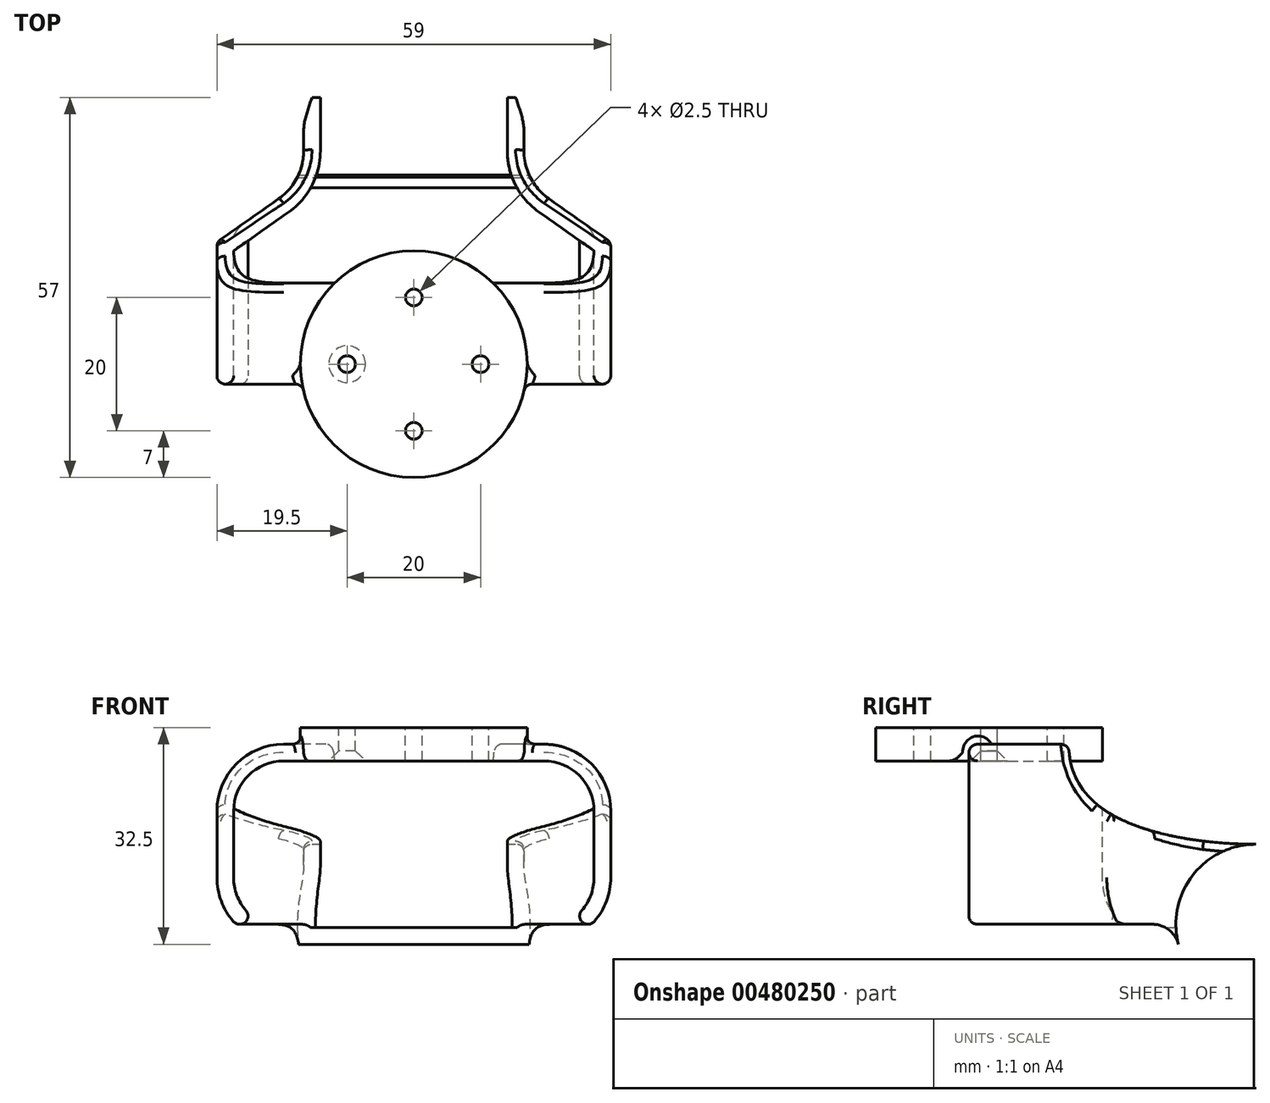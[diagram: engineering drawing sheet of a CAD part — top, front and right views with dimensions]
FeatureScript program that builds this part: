
annotation { "Feature Type Name" : "Feature", "Feature Type Description" : "" }
export const myFeature = defineFeature(function(context is Context, id is Id, definition is map)
    precondition{}
    {
        {
            var Q0;
            Q0=qCreatedBy(makeId("Right.planeOp"),FACE);
            var sketch = newSketch(context, id + "F0", { "sketchPlane" : qUnion([Q0])});
            skCircle(sketch, "E0", {"center": v(8, -12) * mm, "radius": 12 * mm});
            skCircle(sketch, "E1", {"center": v(8, -12) * mm, "radius": 9.5 * mm});
            skSolve(sketch);
        }
        {
            var Q0;
            Q0 = qSketchRegion(id + "F0", true);
            extrude(context, id + "F1", {"entities" : qUnion([Q0]), "endBound" : BoundingType.SYMMETRIC, "depth" : 50 * mm});
        }
        {
            var Q0;
            Q0=qCreatedBy(makeId("Top.planeOp"),FACE);
            var sketch = newSketch(context, id + "F2", { "sketchPlane" : qUnion([Q0])});
            skLineSegment(sketch, "E2", {"start": v(27, -15) * mm, "end": v(27, -35) * mm});
            skArc(sketch, "E3", {"start": v(14, 0) * mm, "mid": v(15.28, -5.22) * mm, "end": v(18.81, -9.26) * mm});
            skLineSegment(sketch, "E4", {"start": v(18.81, -9.26) * mm, "end": v(27, -15) * mm});
            skLineSegment(sketch, "E5", {"start": v(14, 0) * mm, "end": v(14, 20) * mm});
            skLineSegment(sketch, "E6", {"start": v(14, 20) * mm, "end": v(0, 20) * mm});
            skLineSegment(sketch, "E7.0", {"start": v(29.5, 22.5) * mm, "end": v(0, 22.5) * mm});
            skLineSegment(sketch, "E7.1", {"start": v(29.5, 22.5) * mm, "end": v(29.5, -35) * mm});
            skLineSegment(sketch, "E8", {"start": v(0, 22.5) * mm, "end": v(0, -35) * mm});
            skLineSegment(sketch, "E9", {"start": v(0, -35) * mm, "end": v(29.5, -35) * mm});
            skLineSegment(sketch, "E10.MirrorCS", {"start": v(-29.5, 22.5) * mm, "end": v(0, 22.5) * mm});
            skLineSegment(sketch, "E11.MirrorCS", {"start": v(-29.5, 22.5) * mm, "end": v(-29.5, -35) * mm});
            skLineSegment(sketch, "E12.MirrorCS", {"start": v(0, -35) * mm, "end": v(-29.5, -35) * mm});
            skSolve(sketch);
        }
        {
            var Q0;
            Q0 = qSketchRegion(id + "F2", true);
            extrude(context, id + "F3", {"entities" : qUnion([Q0]), "endBound" : BoundingType.SYMMETRIC, "depth" : 30 * mm});
        }
        {
            var Q0;
            Q0=makeQuery(id+"F3.opExtrude","CAP_EDGE",EDGE,{"disambiguationData":[OSD([sQuery(id+"F2.wireOp",EDGE,"E7.1")])],"isStart":false});
            var Q1;
            Q1=makeQuery(id+"F3.opExtrude","CAP_EDGE",EDGE,{"disambiguationData":[OSD([sQuery(id+"F2.wireOp",EDGE,"E7.1")])],"isStart":true});
            var Q2;
            Q2=makeQuery(id+"F3.opExtrude","CAP_EDGE",EDGE,{"disambiguationData":[OSD([sQuery(id+"F2.wireOp",EDGE,"E11.MirrorCS")])],"isStart":false});
            var Q3;
            Q3=makeQuery(id+"F3.opExtrude","CAP_EDGE",EDGE,{"disambiguationData":[OSD([sQuery(id+"F2.wireOp",EDGE,"E11.MirrorCS")])],"isStart":true});
            fillet(context, id + "F4", {"entities" : qUnion([Q0, Q1, Q2, Q3]), "radius" : 10 * mm, "tangentPropagation" : true, "allowEdgeOverflow" : false});
        }
        {
            var Q0;
            Q0=qCreatedBy(makeId("Top.planeOp"),FACE);
            var sketch = newSketch(context, id + "F5", { "sketchPlane" : qUnion([Q0])});
            skLineSegment(sketch, "E13", {"start": v(27, -15) * mm, "end": v(27, -35) * mm});
            skArc(sketch, "E14", {"start": v(14, 0) * mm, "mid": v(15.28, -5.22) * mm, "end": v(18.81, -9.26) * mm});
            skLineSegment(sketch, "E15", {"start": v(18.81, -9.26) * mm, "end": v(27, -15) * mm});
            skLineSegment(sketch, "E16", {"start": v(14, 0) * mm, "end": v(14, 22.5) * mm});
            skLineSegment(sketch, "E17.0", {"start": v(16.5, 0) * mm, "end": v(16.5, 22.5) * mm});
            skArc(sketch, "E17.1", {"start": v(16.5, 0) * mm, "mid": v(17.5, -4.06) * mm, "end": v(20.25, -7.21) * mm});
            skLineSegment(sketch, "E17.2", {"start": v(20.25, -7.21) * mm, "end": v(29.5, -13.7) * mm});
            skLineSegment(sketch, "E18", {"start": v(16.5, 22.5) * mm, "end": v(29.5, 22.5) * mm});
            skLineSegment(sketch, "E19", {"start": v(29.5, 22.5) * mm, "end": v(29.5, -13.7) * mm});
            skLineSegment(sketch, "E20.MirrorCS", {"start": v(-16.5, 0) * mm, "end": v(-16.5, 22.5) * mm});
            skLineSegment(sketch, "E21.MirrorCS", {"start": v(-16.5, 22.5) * mm, "end": v(-29.5, 22.5) * mm});
            skLineSegment(sketch, "E22.MirrorCS", {"start": v(-29.5, 22.5) * mm, "end": v(-29.5, -13.7) * mm});
            skArc(sketch, "E23.MirrorCS", {"start": v(-16.5, 0) * mm, "mid": v(-17.5, -4.06) * mm, "end": v(-20.25, -7.21) * mm});
            skLineSegment(sketch, "E24.MirrorCS", {"start": v(-20.25, -7.21) * mm, "end": v(-29.5, -13.7) * mm});
            skSolve(sketch);
        }
        {
            var Q0;
            Q0 = qSketchRegion(id + "F5", true);
            extrude(context, id + "F6", {"entities" : qUnion([Q0]), "operationType" : NewBodyOperationType.REMOVE, "endBound" : BoundingType.SYMMETRIC, "oppositeDirection" : true, "depth" : 50 * mm});
        }
        {
            var Q0;
            {var subQ0=makeQuery(id+"F3.opExtrude","SWEPT_FACE",FACE,{"disambiguationData":[OSD([sQuery(id+"F2.wireOp",EDGE,"E9")])]});Q0=makeQuery(id+"F3nsgiuGHSw1DEI_1.boolean.opBoolean","MERGE",FACE,{"derivedFrom":[subQ0,makeQuery(id+"F3nsgiuGHSw1DEI_1.opPattern","COPY",FACE,{"derivedFrom":subQ0,"instanceName":"1"})]});}
            shell(context, id + "F7", {"entities" : qUnion([Q0]), "thickness" : 2.5 * mm});
        }
        {
            var Q0;
            Q0=qCreatedBy(makeId("Right.planeOp"),FACE);
            var sketch = newSketch(context, id + "F8", { "sketchPlane" : qUnion([Q0])});
            skFitSpline(sketch, "E25", {"points": [v(-20, 15) * mm, v(-14.5, 5) * mm, v(8, 0) * mm], "startDerivative": vector(-1.27, -29.05) * mm, "endDerivative": vector(40.9, 0) * mm});
            skLineSegment(sketch, "E26", {"start": v(-20, 15) * mm, "end": v(-20, 23.6) * mm});
            skLineSegment(sketch, "E27", {"start": v(-20.04, 21.23) * mm, "end": v(28.46, 21.23) * mm});
            skLineSegment(sketch, "E28", {"start": v(28.46, 21.23) * mm, "end": v(28.46, -29.42) * mm});
            skLineSegment(sketch, "E29", {"start": v(28.46, -29.42) * mm, "end": v(-37.88, -29.42) * mm});
            skLineSegment(sketch, "E30", {"start": v(-37.88, -12) * mm, "end": v(-7.5, -12) * mm});
            skArc(sketch, "E31", {"start": v(-3.62, -15) * mm, "mid": v(-5.04, -12.84) * mm, "end": v(-7.5, -12) * mm});
            skLineSegment(sketch, "E32", {"start": v(-37.88, -12) * mm, "end": v(-37.88, -29.42) * mm});
            skLineSegment(sketch, "E33", {"start": v(8, 0) * mm, "end": v(8, -12) * mm});
            skCircle(sketch, "E34", {"center": v(8, -12) * mm, "radius": 12 * mm});
            skSolve(sketch);
        }
        {
            var Q0;
            Q0 = qSketchRegion(id + "F8", true);
            extrude(context, id + "F9", {"entities" : qUnion([Q0]), "operationType" : NewBodyOperationType.REMOVE, "endBound" : BoundingType.SYMMETRIC, "oppositeDirection" : true, "depth" : 60 * mm});
        }
        {
            var Q0;
            {var subQ0=sQuery(id+"F2.wireOp",EDGE,"E12.MirrorCS");var subQ1=sQuery(id+"F2.wireOp",EDGE,"E11.MirrorCS");var subQ2=sQuery(id+"F2.wireOp",EDGE,"E10.MirrorCS");var subQ3=sQuery(id+"F2.wireOp",EDGE,"E9");var subQ4=sQuery(id+"F2.wireOp",EDGE,"E7.1");var subQ5=sQuery(id+"F2.wireOp",EDGE,"E7.0");Q0=makeQuery(id+"F7.opShell","OFFSET_FACE",FACE,{"disambiguationData":[OSD([subQ5,subQ4,subQ3,subQ2,subQ1,subQ0]),TDD([makeQuery(id+"F3.opExtrude","CAP_FACE",FACE,{"disambiguationData":[OSD([subQ5,subQ4,subQ3,subQ2,subQ1,subQ0])],"isStart":false})])]});}
            var sketch = newSketch(context, id + "F10", { "sketchPlane" : qUnion([Q0])});
            skCircle(sketch, "E35", {"center": v(0, 32) * mm, "radius": 17 * mm});
            skPoint(sketch, "E35.centerSnap0", {"position": v(0, 20) * mm});
            skCircle(sketch, "E36", {"center": v(0, 32) * mm, "radius": 15 * mm, "construction": true});
            skSolve(sketch);
        }
        {
            var Q0;
            Q0 = qSketchRegion(id + "F10", true);
            extrude(context, id + "F11", {"entities" : qUnion([Q0]), "operationType" : NewBodyOperationType.ADD, "oppositeDirection" : true, "depth" : 5 * mm});
        }
        {
            var Q0;
            Q0=makeQuery(id+"F11.opExtrude","CAP_FACE",FACE,{"disambiguationData":[OSD([sQuery(id+"F10.wireOp",EDGE,"E35")])],"isStart":false});
            var sketch = newSketch(context, id + "F12", { "sketchPlane" : qUnion([Q0])});
            skCircle(sketch, "E37", {"center": v(-10, -32) * mm, "radius": 1.25 * mm});
            skLineSegment(sketch, "E38", {"start": v(-17, -32) * mm, "end": v(0, -32) * mm, "construction": true});
            skCircle(sketch, "E39.1.0", {"center": v(0, -42) * mm, "radius": 1.25 * mm});
            skCircle(sketch, "E39.2.0", {"center": v(10, -32) * mm, "radius": 1.25 * mm});
            skCircle(sketch, "E39.3.0", {"center": v(0, -22) * mm, "radius": 1.25 * mm});
            skPoint(sketch, "E39.center", {"position": v(0, -32) * mm});
            skSolve(sketch);
        }
        {
            var Q0;
            Q0 = qSketchRegion(id + "F12", true);
            extrude(context, id + "F13", {"entities" : qUnion([Q0]), "operationType" : NewBodyOperationType.REMOVE, "oppositeDirection" : true, "depth" : 10 * mm});
        }
        {
            var Q0;
            {var subQ0=sQuery(id+"F2.wireOp",EDGE,"E12.MirrorCS");var subQ1=sQuery(id+"F2.wireOp",EDGE,"E11.MirrorCS");var subQ2=sQuery(id+"F2.wireOp",EDGE,"E10.MirrorCS");var subQ3=sQuery(id+"F2.wireOp",EDGE,"E9");var subQ4=sQuery(id+"F2.wireOp",EDGE,"E7.1");var subQ5=sQuery(id+"F2.wireOp",EDGE,"E7.0");Q0=makeQuery(id+"F13.boolean.opBoolean","INTERSECT",EDGE,{"derivedFrom":[makeQuery(id+"F11.boolean.opBoolean","MERGE",FACE,{"derivedFrom":[makeQuery(id+"F7.opShell","OFFSET_FACE",FACE,{"disambiguationData":[OSD([subQ5,subQ4,subQ3,subQ2,subQ1,subQ0]),TDD([makeQuery(id+"F3.opExtrude","CAP_FACE",FACE,{"disambiguationData":[OSD([subQ5,subQ4,subQ3,subQ2,subQ1,subQ0])],"isStart":false})])]}),makeQuery(id+"F11.opExtrude","CAP_FACE",FACE,{"disambiguationData":[OSD([sQuery(id+"F10.wireOp",EDGE,"E35")])],"isStart":true})]}),makeQuery(id+"F13.opExtrude","SWEPT_FACE",FACE,{"disambiguationData":[OSD([sQuery(id+"F12.wireOp",EDGE,"E37")])]})]});}
            var Q1;
            {var subQ0=sQuery(id+"F2.wireOp",EDGE,"E12.MirrorCS");var subQ1=sQuery(id+"F2.wireOp",EDGE,"E11.MirrorCS");var subQ2=sQuery(id+"F2.wireOp",EDGE,"E10.MirrorCS");var subQ3=sQuery(id+"F2.wireOp",EDGE,"E9");var subQ4=sQuery(id+"F2.wireOp",EDGE,"E7.1");var subQ5=sQuery(id+"F2.wireOp",EDGE,"E7.0");Q1=makeQuery(id+"F13.boolean.opBoolean","INTERSECT",EDGE,{"derivedFrom":[makeQuery(id+"F11.boolean.opBoolean","MERGE",FACE,{"derivedFrom":[makeQuery(id+"F7.opShell","OFFSET_FACE",FACE,{"disambiguationData":[OSD([subQ5,subQ4,subQ3,subQ2,subQ1,subQ0]),TDD([makeQuery(id+"F3.opExtrude","CAP_FACE",FACE,{"disambiguationData":[OSD([subQ5,subQ4,subQ3,subQ2,subQ1,subQ0])],"isStart":false})])]}),makeQuery(id+"F11.opExtrude","CAP_FACE",FACE,{"disambiguationData":[OSD([sQuery(id+"F10.wireOp",EDGE,"E35")])],"isStart":true})]}),makeQuery(id+"F13.opExtrude","SWEPT_FACE",FACE,{"disambiguationData":[OSD([sQuery(id+"F12.wireOp",EDGE,"b85b92ab-dbc8-460f-88aa-ae4718680d460.MirrorC")])]})]});}
            chamfer(context, id + "F14", {"entities" : qUnion([Q0, Q1]), "width" : 1.5 * mm, "tangentPropagation" : true});
        }
        {
            var Q0;
            {var subQ0=sQuery(id+"F2.wireOp",EDGE,"E11.MirrorCS");Q0=makeQuery(id+"F9.boolean.opBoolean","INTERSECT",EDGE,{"derivedFrom":[makeQuery(id+"F7.opShell","OFFSET_FACE",FACE,{"disambiguationData":[OSD([subQ0]),TDD([makeQuery(id+"F4.opFillet","BLEND_FACE",FACE,{"disambiguationData":[OSD([subQ0]),TDD([makeQuery(id+"F3.opExtrude","CAP_EDGE",EDGE,{"disambiguationData":[OSD([subQ0])],"isStart":true})])]})])]}),makeQuery(id+"F9.opExtrude","SWEPT_FACE",FACE,{"disambiguationData":[OSD([sQuery(id+"F8.wireOp",EDGE,"E30")])]})]});}
            var Q1;
            {var subQ0=sQuery(id+"F2.wireOp",EDGE,"E11.MirrorCS");Q1=makeQuery(id+"F9.boolean.opBoolean","INTERSECT",EDGE,{"derivedFrom":[makeQuery(id+"F4.opFillet","BLEND_FACE",FACE,{"disambiguationData":[OSD([subQ0]),TDD([makeQuery(id+"F3.opExtrude","CAP_EDGE",EDGE,{"disambiguationData":[OSD([subQ0])],"isStart":true})])]}),makeQuery(id+"F9.opExtrude","SWEPT_FACE",FACE,{"disambiguationData":[OSD([sQuery(id+"F8.wireOp",EDGE,"E30")])]})]});}
            var Q2;
            {var subQ0=sQuery(id+"F2.wireOp",EDGE,"E7.1");Q2=makeQuery(id+"F9.boolean.opBoolean","INTERSECT",EDGE,{"derivedFrom":[makeQuery(id+"F7.opShell","OFFSET_FACE",FACE,{"disambiguationData":[OSD([subQ0]),TDD([makeQuery(id+"F4.opFillet","BLEND_FACE",FACE,{"disambiguationData":[OSD([subQ0]),TDD([makeQuery(id+"F3.opExtrude","CAP_EDGE",EDGE,{"disambiguationData":[OSD([subQ0])],"isStart":true})])]})])]}),makeQuery(id+"F9.opExtrude","SWEPT_FACE",FACE,{"disambiguationData":[OSD([sQuery(id+"F8.wireOp",EDGE,"E30")])]})]});}
            var Q3;
            {var subQ0=sQuery(id+"F2.wireOp",EDGE,"E7.1");Q3=makeQuery(id+"F9.boolean.opBoolean","INTERSECT",EDGE,{"derivedFrom":[makeQuery(id+"F4.opFillet","BLEND_FACE",FACE,{"disambiguationData":[OSD([subQ0]),TDD([makeQuery(id+"F3.opExtrude","CAP_EDGE",EDGE,{"disambiguationData":[OSD([subQ0])],"isStart":true})])]}),makeQuery(id+"F9.opExtrude","SWEPT_FACE",FACE,{"disambiguationData":[OSD([sQuery(id+"F8.wireOp",EDGE,"E30")])]})]});}
            var Q4;
            {var subQ2=sQuery(id+"F2.wireOp",EDGE,"E11.MirrorCS");var subQ5=sQuery(id+"F2.wireOp",EDGE,"E12.MirrorCS");var subQ6=sQuery(id+"F2.wireOp",EDGE,"E9");var subQ7=makeQuery(id+"F3.opExtrude","SWEPT_FACE",FACE,{"disambiguationData":[OSD([subQ6,subQ5])]});var subQ8=makeQuery(id+"F3.opExtrude","SWEPT_FACE",FACE,{"disambiguationData":[OSD([subQ2])]});Q4=makeQuery(id+"F11.boolean.opBoolean","SPLIT",FACE,{"disambiguationData":[TD([subQ8])],"derivedFrom":subQ7});}
            var Q5;
            {var subQ1=sQuery(id+"F2.wireOp",EDGE,"E7.1");var subQ2=makeQuery(id+"F3.opExtrude","SWEPT_FACE",FACE,{"disambiguationData":[OSD([subQ1])]});var subQ3=sQuery(id+"F2.wireOp",EDGE,"E12.MirrorCS");var subQ6=sQuery(id+"F2.wireOp",EDGE,"E9");var subQ13=makeQuery(id+"F3.opExtrude","SWEPT_FACE",FACE,{"disambiguationData":[OSD([subQ6,subQ3])]});Q5=makeQuery(id+"F11.boolean.opBoolean","SPLIT",FACE,{"disambiguationData":[TD([subQ2])],"derivedFrom":subQ13});}
            var Q6;
            Q6=makeQuery(id+"F6.boolean.opBoolean","COPY",EDGE,{"derivedFrom":makeQuery(id+"F6.opExtrude","SWEPT_EDGE",EDGE,{"disambiguationData":[OSD([sQuery(id+"F5.wireOp",EDGE,"E17.2"),sQuery(id+"F5.wireOp",EDGE,"E19")])]})});
            var Q7;
            {var subQ0=sQuery(id+"F2.wireOp",EDGE,"E7.1");Q7=makeQuery(id+"F6.boolean.opBoolean","INTERSECT",EDGE,{"derivedFrom":[makeQuery(id+"F4.opFillet","BLEND_FACE",FACE,{"disambiguationData":[OSD([subQ0]),TDD([makeQuery(id+"F3.opExtrude","CAP_EDGE",EDGE,{"disambiguationData":[OSD([subQ0])],"isStart":true})])]}),makeQuery(id+"F6.opExtrude","SWEPT_FACE",FACE,{"disambiguationData":[OSD([sQuery(id+"F5.wireOp",EDGE,"E17.2")])]})]});}
            var Q8;
            Q8=makeQuery(id+"F6.boolean.opBoolean","COPY",EDGE,{"derivedFrom":makeQuery(id+"F6.opExtrude","SWEPT_EDGE",EDGE,{"disambiguationData":[OSD([sQuery(id+"F5.wireOp",EDGE,"E22.MirrorCS"),sQuery(id+"F5.wireOp",EDGE,"E24.MirrorCS")])]})});
            var Q9;
            {var subQ0=sQuery(id+"F2.wireOp",EDGE,"E11.MirrorCS");Q9=makeQuery(id+"F6.boolean.opBoolean","INTERSECT",EDGE,{"derivedFrom":[makeQuery(id+"F4.opFillet","BLEND_FACE",FACE,{"disambiguationData":[OSD([subQ0]),TDD([makeQuery(id+"F3.opExtrude","CAP_EDGE",EDGE,{"disambiguationData":[OSD([subQ0])],"isStart":true})])]}),makeQuery(id+"F6.opExtrude","SWEPT_FACE",FACE,{"disambiguationData":[OSD([sQuery(id+"F5.wireOp",EDGE,"E24.MirrorCS")])]})]});}
            var Q10;
            {var subQ0=sQuery(id+"F2.wireOp",EDGE,"E7.1");Q10=makeQuery(id+"F9.boolean.opBoolean","INTERSECT",EDGE,{"derivedFrom":[makeQuery(id+"F4.opFillet","BLEND_FACE",FACE,{"disambiguationData":[OSD([subQ0]),TDD([makeQuery(id+"F3.opExtrude","CAP_EDGE",EDGE,{"disambiguationData":[OSD([subQ0])],"isStart":false})])]}),makeQuery(id+"F9.opExtrude","SWEPT_FACE",FACE,{"disambiguationData":[OSD([sQuery(id+"F8.wireOp",EDGE,"E25")])]})]});}
            var Q11;
            Q11=makeQuery(id+"F9.boolean.opBoolean","INTERSECT",EDGE,{"derivedFrom":[makeQuery(id+"F6.boolean.opBoolean","COPY",FACE,{"derivedFrom":makeQuery(id+"F6.opExtrude","SWEPT_FACE",FACE,{"disambiguationData":[OSD([sQuery(id+"F5.wireOp",EDGE,"E17.2")])]})}),makeQuery(id+"F9.opExtrude","SWEPT_FACE",FACE,{"disambiguationData":[OSD([sQuery(id+"F8.wireOp",EDGE,"E25")])]})]});
            var Q12;
            {var subQ0=sQuery(id+"F2.wireOp",EDGE,"E11.MirrorCS");Q12=makeQuery(id+"F9.boolean.opBoolean","INTERSECT",EDGE,{"derivedFrom":[makeQuery(id+"F4.opFillet","BLEND_FACE",FACE,{"disambiguationData":[OSD([subQ0]),TDD([makeQuery(id+"F3.opExtrude","CAP_EDGE",EDGE,{"disambiguationData":[OSD([subQ0])],"isStart":false})])]}),makeQuery(id+"F9.opExtrude","SWEPT_FACE",FACE,{"disambiguationData":[OSD([sQuery(id+"F8.wireOp",EDGE,"E25")])]})]});}
            var Q13;
            Q13=makeQuery(id+"F9.boolean.opBoolean","INTERSECT",EDGE,{"derivedFrom":[makeQuery(id+"F6.boolean.opBoolean","COPY",FACE,{"derivedFrom":makeQuery(id+"F6.opExtrude","SWEPT_FACE",FACE,{"disambiguationData":[OSD([sQuery(id+"F5.wireOp",EDGE,"E24.MirrorCS")])]})}),makeQuery(id+"F9.opExtrude","SWEPT_FACE",FACE,{"disambiguationData":[OSD([sQuery(id+"F8.wireOp",EDGE,"E25")])]})]});
            fillet(context, id + "F15", {"entities" : qUnion([Q0, Q1, Q2, Q3, Q4, Q5, Q6, Q7, Q8, Q9, Q10, Q11, Q12, Q13]), "radius" : 1.25 * mm, "tangentPropagation" : true, "allowEdgeOverflow" : false});
        }
    });
